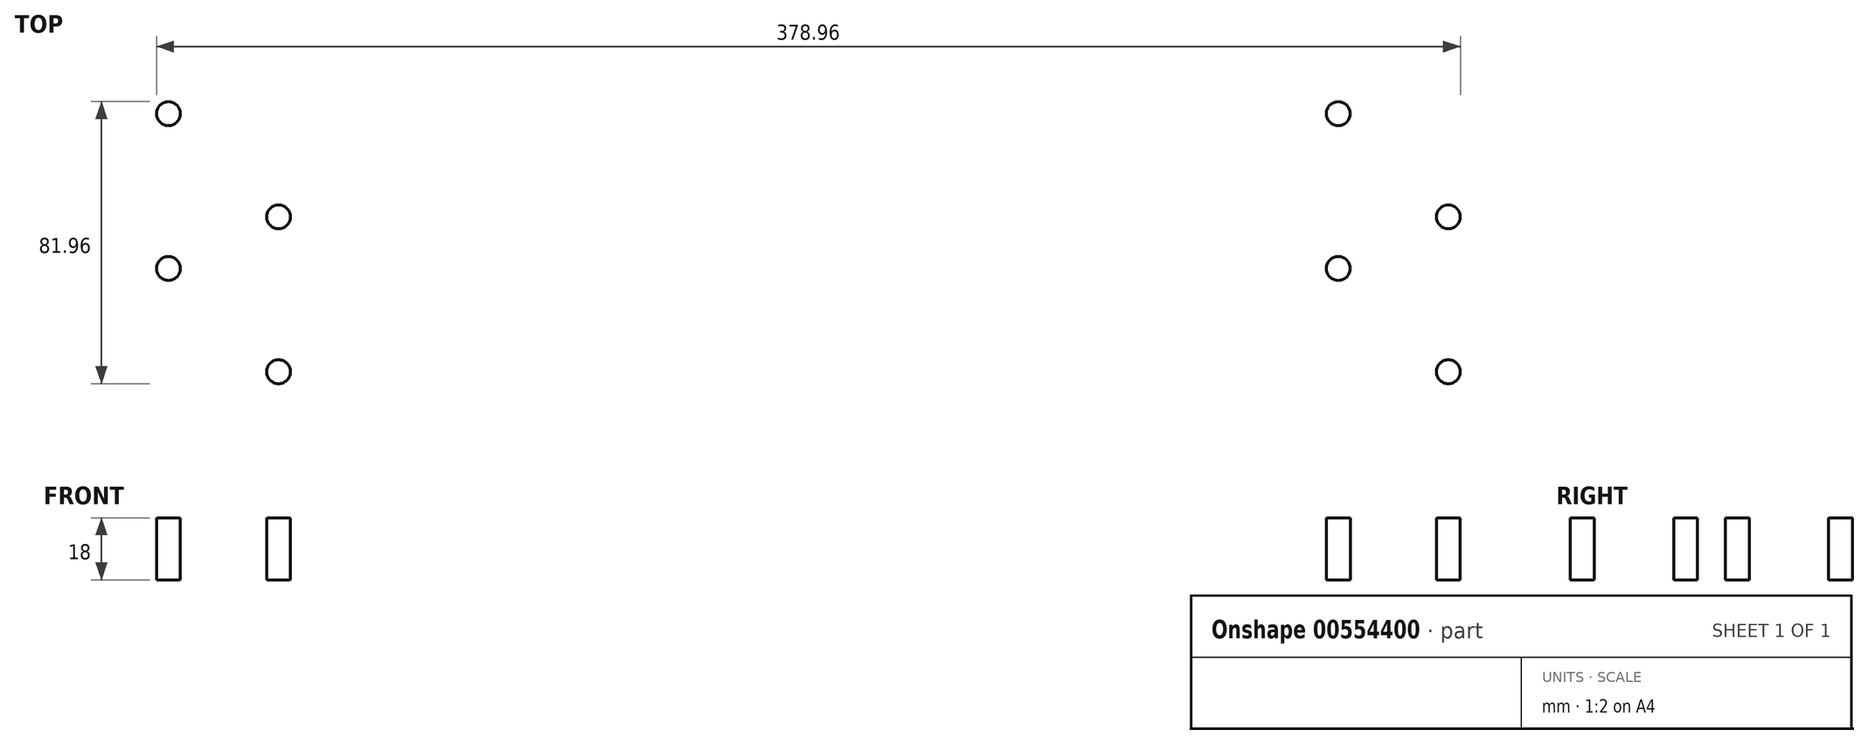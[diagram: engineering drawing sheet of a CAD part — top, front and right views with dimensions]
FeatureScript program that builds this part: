
annotation { "Feature Type Name" : "Feature", "Feature Type Description" : "" }
export const myFeature = defineFeature(function(context is Context, id is Id, definition is map)
    precondition{}
    {
        {
            var Q0;
            Q0=qCreatedBy(makeId("Top.planeOp"),FACE);
            var sketch = newSketch(context, id + "F0", { "sketchPlane" : qUnion([Q0])});
            skLineSegment(sketch, "E0.bottom", {"start": v(0, 0) * mm, "end": v(1000, 0) * mm});
            skLineSegment(sketch, "E0.top", {"start": v(0, 500) * mm, "end": v(1000, 500) * mm});
            skLineSegment(sketch, "E0.left", {"start": v(0, 0) * mm, "end": v(0, 500) * mm});
            skLineSegment(sketch, "E0.right", {"start": v(1000, 0) * mm, "end": v(1000, 500) * mm});
            skSolve(sketch);
        }
        {
            var Q0;
            Q0=makeQuery(id+"F0.imprint","IMPRINT",FACE,{"disambiguationData":[TD([[makeQuery(id+"F0.imprint","IMPRINT",EDGE,{"derivedFrom":sQuery(id+"F0.wireOp",EDGE,"E0.bottom")}),1.0]])]});
            extrude(context, id + "F1", {"entities" : qUnion([Q0]), "depth" : 18 * mm, "offsetDistance" : 25 * mm});
        }
        {
            var Q0;
            Q0=makeQuery(id+"F1.opExtrude","CAP_FACE",FACE,{"disambiguationData":[OSD([sQuery(id+"F0.wireOp",EDGE,"E0.bottom"),sQuery(id+"F0.wireOp",EDGE,"E0.top"),sQuery(id+"F0.wireOp",EDGE,"E0.left"),sQuery(id+"F0.wireOp",EDGE,"E0.right")])],"isStart":false});
            var sketch = newSketch(context, id + "F2", { "sketchPlane" : qUnion([Q0])});
            skLineSegment(sketch, "E1", {"start": v(670, 104.98) * mm, "end": v(670, 362.58) * mm});
            skLineSegment(sketch, "E2", {"start": v(330, 107.96) * mm, "end": v(330, 380.94) * mm});
            skLineSegment(sketch, "E3", {"start": v(865.66, 250) * mm, "end": v(142.21, 250) * mm});
            skSolve(sketch);
        }
        {
            var Q0;
            Q0=makeQuery(id+"F2.imprint","IMPRINT",FACE,{"disambiguationData":[TD([[makeQuery(id+"F2.imprint","IMPRINT",EDGE,{"derivedFrom":makeQuery(id+"F1.opExtrude","CAP_EDGE",EDGE,{"disambiguationData":[OSD([sQuery(id+"F0.wireOp",EDGE,"E0.bottom")])],"isStart":false})}),1.0]])]});
            var sketch = newSketch(context, id + "F3", { "sketchPlane" : qUnion([Q0])});
            skLineSegment(sketch, "E4", {"start": v(310, 266.64) * mm, "end": v(310, 216.55) * mm});
            skLineSegment(sketch, "E5", {"start": v(690, 292.39) * mm, "end": v(690, 159.53) * mm});
            skLineSegment(sketch, "E6", {"start": v(0, 250) * mm, "end": v(970.77, 250) * mm, "construction": true});
            skLineSegment(sketch, "E7.0", {"start": v(0, 0) * mm, "end": v(0, 500) * mm});
            skLineSegment(sketch, "E8.0", {"start": v(330, 107.96) * mm, "end": v(330, 380.94) * mm, "construction": true});
            skLineSegment(sketch, "E9.0", {"start": v(670, 104.98) * mm, "end": v(670, 362.58) * mm, "construction": true});
            skLineSegment(sketch, "E10", {"start": v(350.67, 272.5) * mm, "end": v(312.06, 272.5) * mm});
            skCircle(sketch, "E11", {"center": v(314, 257.5) * mm, "radius": 3.48 * mm});
            skCircle(sketch, "E12.MirrorC", {"center": v(346, 257.5) * mm, "radius": 3.48 * mm});
            skCircle(sketch, "E13.MirrorC", {"center": v(314, 287.5) * mm, "radius": 3.48 * mm});
            skCircle(sketch, "E14.MirrorC", {"center": v(346, 287.5) * mm, "radius": 3.48 * mm});
            skCircle(sketch, "E15.MirrorC", {"center": v(346, 242.5) * mm, "radius": 3.48 * mm});
            skCircle(sketch, "E16.MirrorC", {"center": v(314, 242.5) * mm, "radius": 3.48 * mm});
            skCircle(sketch, "E17.MirrorC", {"center": v(314, 212.5) * mm, "radius": 3.48 * mm});
            skCircle(sketch, "E18.MirrorC", {"center": v(346, 212.5) * mm, "radius": 3.48 * mm});
            skLineSegment(sketch, "E19.0", {"start": v(0, 500) * mm, "end": v(1000, 500) * mm});
            skLineSegment(sketch, "E20.0", {"start": v(0, 0) * mm, "end": v(1000, 0) * mm});
            skLineSegment(sketch, "E21", {"start": v(500, 500) * mm, "end": v(500, 0) * mm});
            skCircle(sketch, "E22.MirrorC", {"center": v(654, 212.5) * mm, "radius": 3.48 * mm});
            skCircle(sketch, "E23.MirrorC", {"center": v(686, 212.5) * mm, "radius": 3.48 * mm});
            skCircle(sketch, "E24.MirrorC", {"center": v(686, 242.5) * mm, "radius": 3.48 * mm});
            skCircle(sketch, "E25.MirrorC", {"center": v(654, 242.5) * mm, "radius": 3.48 * mm});
            skCircle(sketch, "E26.MirrorC", {"center": v(654, 257.5) * mm, "radius": 3.48 * mm});
            skCircle(sketch, "E27.MirrorC", {"center": v(686, 257.5) * mm, "radius": 3.48 * mm});
            skCircle(sketch, "E28.MirrorC", {"center": v(686, 287.5) * mm, "radius": 3.48 * mm});
            skCircle(sketch, "E29.MirrorC", {"center": v(654, 287.5) * mm, "radius": 3.48 * mm});
            skSolve(sketch);
        }
        {
            var Q0;
            Q0=makeQuery(id+"F3.imprint","IMPRINT",FACE,{"disambiguationData":[TD([[makeQuery(id+"F3.imprint","IMPRINT",EDGE,{"derivedFrom":sQuery(id+"F3.wireOp",EDGE,"E18.MirrorC")}),-1.0]])]});
            var Q1;
            Q1=makeQuery(id+"F3.imprint","IMPRINT",FACE,{"disambiguationData":[TD([[makeQuery(id+"F3.imprint","IMPRINT",EDGE,{"derivedFrom":sQuery(id+"F3.wireOp",EDGE,"E17.MirrorC")}),1.0]])]});
            var Q2;
            Q2=makeQuery(id+"F3.imprint","IMPRINT",FACE,{"disambiguationData":[TD([[makeQuery(id+"F3.imprint","IMPRINT",EDGE,{"derivedFrom":sQuery(id+"F3.wireOp",EDGE,"E16.MirrorC")}),-1.0]])]});
            var Q3;
            Q3=makeQuery(id+"F3.imprint","IMPRINT",FACE,{"disambiguationData":[TD([[makeQuery(id+"F3.imprint","IMPRINT",EDGE,{"derivedFrom":sQuery(id+"F3.wireOp",EDGE,"E15.MirrorC")}),1.0]])]});
            var Q4;
            Q4=makeQuery(id+"F3.imprint","IMPRINT",FACE,{"disambiguationData":[TD([[makeQuery(id+"F3.imprint","IMPRINT",EDGE,{"derivedFrom":sQuery(id+"F3.wireOp",EDGE,"E12.MirrorC")}),-1.0]])]});
            var Q5;
            Q5=makeQuery(id+"F3.imprint","IMPRINT",FACE,{"disambiguationData":[TD([[makeQuery(id+"F3.imprint","IMPRINT",EDGE,{"derivedFrom":sQuery(id+"F3.wireOp",EDGE,"E11")}),1.0]])]});
            var Q6;
            Q6=makeQuery(id+"F3.imprint","IMPRINT",FACE,{"disambiguationData":[TD([[makeQuery(id+"F3.imprint","IMPRINT",EDGE,{"derivedFrom":sQuery(id+"F3.wireOp",EDGE,"E13.MirrorC")}),-1.0]])]});
            var Q7;
            Q7=makeQuery(id+"F3.imprint","IMPRINT",FACE,{"disambiguationData":[TD([[makeQuery(id+"F3.imprint","IMPRINT",EDGE,{"derivedFrom":sQuery(id+"F3.wireOp",EDGE,"E14.MirrorC")}),1.0]])]});
            var Q8;
            Q8=makeQuery(id+"F3.imprint","IMPRINT",FACE,{"disambiguationData":[TD([[makeQuery(id+"F3.imprint","IMPRINT",EDGE,{"derivedFrom":sQuery(id+"F3.wireOp",EDGE,"E29.MirrorC")}),-1.0]])]});
            var Q9;
            Q9=makeQuery(id+"F3.imprint","IMPRINT",FACE,{"disambiguationData":[TD([[makeQuery(id+"F3.imprint","IMPRINT",EDGE,{"derivedFrom":sQuery(id+"F3.wireOp",EDGE,"E26.MirrorC")}),1.0]])]});
            var Q10;
            Q10=makeQuery(id+"F3.imprint","IMPRINT",FACE,{"disambiguationData":[TD([[makeQuery(id+"F3.imprint","IMPRINT",EDGE,{"derivedFrom":sQuery(id+"F3.wireOp",EDGE,"E25.MirrorC")}),-1.0]])]});
            var Q11;
            Q11=makeQuery(id+"F3.imprint","IMPRINT",FACE,{"disambiguationData":[TD([[makeQuery(id+"F3.imprint","IMPRINT",EDGE,{"derivedFrom":sQuery(id+"F3.wireOp",EDGE,"E22.MirrorC")}),1.0]])]});
            var Q12;
            Q12=makeQuery(id+"F3.imprint","IMPRINT",FACE,{"disambiguationData":[TD([[makeQuery(id+"F3.imprint","IMPRINT",EDGE,{"derivedFrom":sQuery(id+"F3.wireOp",EDGE,"E28.MirrorC")}),1.0]])]});
            var Q13;
            Q13=makeQuery(id+"F3.imprint","IMPRINT",FACE,{"disambiguationData":[TD([[makeQuery(id+"F3.imprint","IMPRINT",EDGE,{"derivedFrom":sQuery(id+"F3.wireOp",EDGE,"E27.MirrorC")}),-1.0]])]});
            var Q14;
            Q14=makeQuery(id+"F3.imprint","IMPRINT",FACE,{"disambiguationData":[TD([[makeQuery(id+"F3.imprint","IMPRINT",EDGE,{"derivedFrom":sQuery(id+"F3.wireOp",EDGE,"E24.MirrorC")}),1.0]])]});
            var Q15;
            Q15=makeQuery(id+"F3.imprint","IMPRINT",FACE,{"disambiguationData":[TD([[makeQuery(id+"F3.imprint","IMPRINT",EDGE,{"derivedFrom":sQuery(id+"F3.wireOp",EDGE,"E23.MirrorC")}),-1.0]])]});
            extrude(context, id + "F4", {"entities" : qUnion([Q0, Q1, Q2, Q3, Q4, Q5, Q6, Q7, Q8, Q9, Q10, Q11, Q12, Q13, Q14, Q15]), "operationType" : NewBodyOperationType.REMOVE, "oppositeDirection" : true, "depth" : 18 * mm, "offsetDistance" : 25 * mm});
        }
    });
